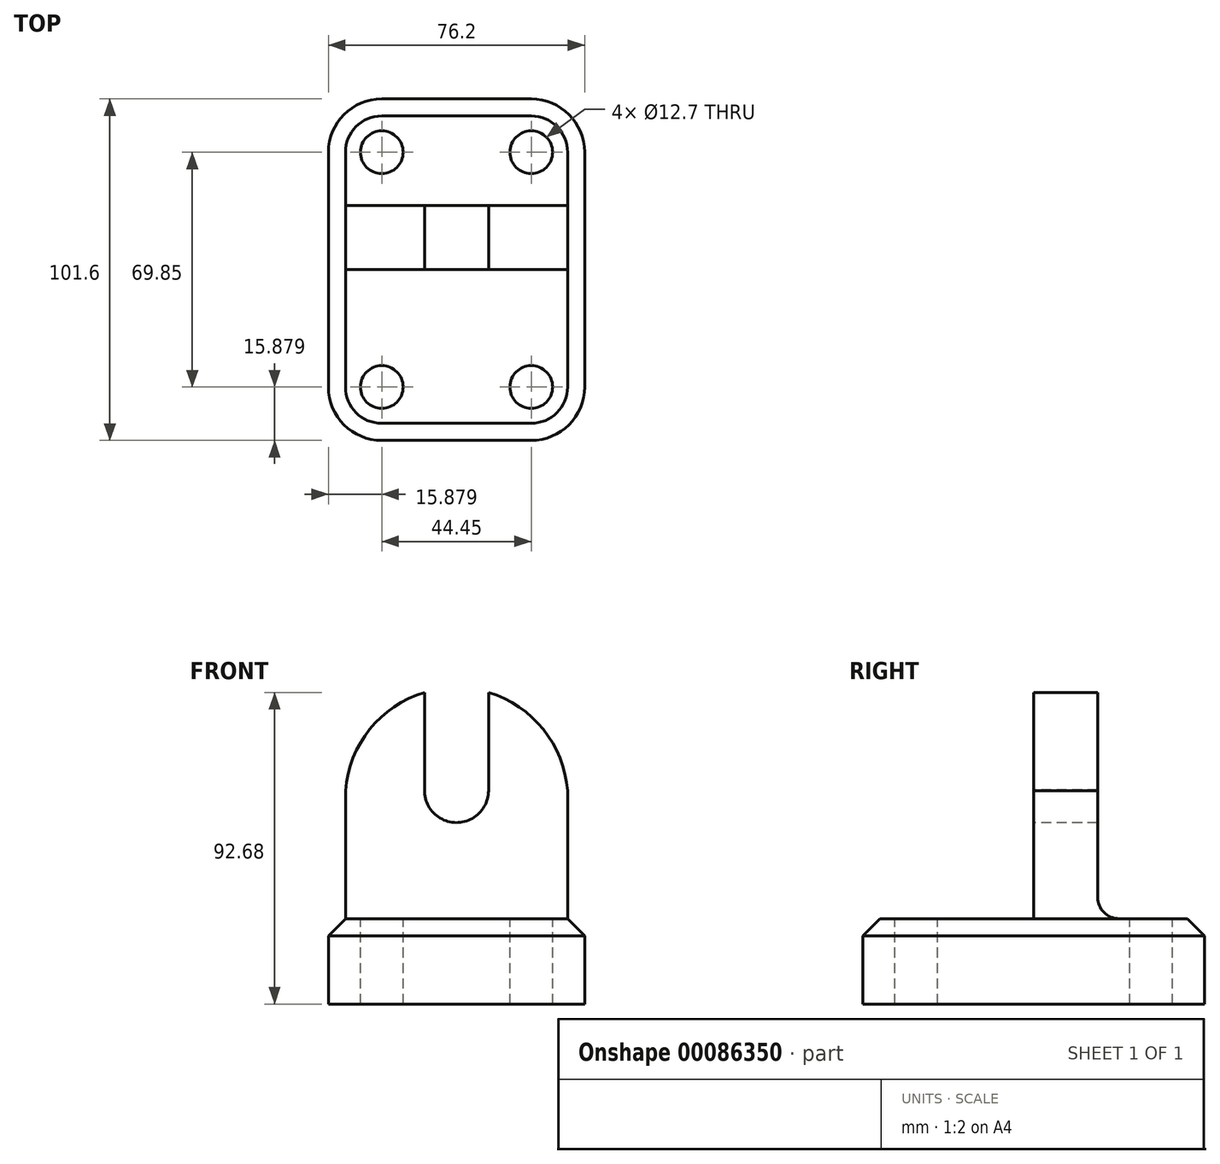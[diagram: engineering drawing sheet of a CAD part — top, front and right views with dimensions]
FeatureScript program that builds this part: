
annotation { "Feature Type Name" : "Feature", "Feature Type Description" : "" }
export const myFeature = defineFeature(function(context is Context, id is Id, definition is map)
    precondition{}
    {
        {
            var Q0;
            Q0=qCreatedBy(makeId("Top.planeOp"),FACE);
            var sketch = newSketch(context, id + "F0", { "sketchPlane" : qUnion([Q0])});
            skLineSegment(sketch, "E0.bottom", {"start": v(-19.44, 54.83) * mm, "end": v(56.76, 54.83) * mm});
            skLineSegment(sketch, "E0.top", {"start": v(-19.44, -46.77) * mm, "end": v(56.76, -46.77) * mm});
            skLineSegment(sketch, "E0.left", {"start": v(-19.44, 54.83) * mm, "end": v(-19.44, -46.77) * mm});
            skLineSegment(sketch, "E0.right", {"start": v(56.76, 54.83) * mm, "end": v(56.76, -46.77) * mm});
            skSolve(sketch);
        }
        {
            var Q0;
            Q0 = qSketchRegion(id + "F0", true);
            extrude(context, id + "F1", {"entities" : qUnion([Q0]), "depth" : 25.4 * mm});
        }
        {
            var Q0;
            Q0=makeQuery(id+"F1.opExtrude","SWEPT_EDGE",EDGE,{"disambiguationData":[OSD([sQuery(id+"F0.wireOp",EDGE,"E0.top"),sQuery(id+"F0.wireOp",EDGE,"E0.left")])]});
            var Q1;
            Q1=makeQuery(id+"F1.opExtrude","SWEPT_EDGE",EDGE,{"disambiguationData":[OSD([sQuery(id+"F0.wireOp",EDGE,"E0.top"),sQuery(id+"F0.wireOp",EDGE,"E0.right")])]});
            var Q2;
            Q2=makeQuery(id+"F1.opExtrude","SWEPT_EDGE",EDGE,{"disambiguationData":[OSD([sQuery(id+"F0.wireOp",EDGE,"E0.bottom"),sQuery(id+"F0.wireOp",EDGE,"E0.right")])]});
            var Q3;
            Q3=makeQuery(id+"F1.opExtrude","SWEPT_EDGE",EDGE,{"disambiguationData":[OSD([sQuery(id+"F0.wireOp",EDGE,"E0.bottom"),sQuery(id+"F0.wireOp",EDGE,"E0.left")])]});
            fillet(context, id + "F2", {"entities" : qUnion([Q0, Q1, Q2, Q3]), "radius" : 15.88 * mm, "tangentPropagation" : true, "allowEdgeOverflow" : false});
        }
        {
            var Q0;
            Q0=makeQuery(id+"F1.opExtrude","CAP_EDGE",EDGE,{"disambiguationData":[OSD([sQuery(id+"F0.wireOp",EDGE,"E0.bottom")])],"isStart":false});
            var Q1;
            {var subQ0=sQuery(id+"F0.wireOp",EDGE,"E0.left");var subQ1=sQuery(id+"F0.wireOp",EDGE,"E0.bottom");Q1=makeQuery(id+"F2.opFillet","BLEND_EDGE",EDGE,{"blendedFrom":[makeQuery(id+"F1.opExtrude","SWEPT_EDGE",EDGE,{"disambiguationData":[OSD([subQ1,subQ0])]}),makeQuery(id+"F1.opExtrude","CAP_FACE",FACE,{"disambiguationData":[OSD([subQ1,sQuery(id+"F0.wireOp",EDGE,"E0.top"),subQ0,sQuery(id+"F0.wireOp",EDGE,"E0.right")])],"isStart":false})],"blendedInto":[makeQuery(id+"F1.opExtrude","CAP_FACE",FACE,{"disambiguationData":[OSD([subQ1,sQuery(id+"F0.wireOp",EDGE,"E0.top"),subQ0,sQuery(id+"F0.wireOp",EDGE,"E0.right")])],"isStart":false})]});}
            var Q2;
            Q2=makeQuery(id+"F1.opExtrude","CAP_EDGE",EDGE,{"disambiguationData":[OSD([sQuery(id+"F0.wireOp",EDGE,"E0.left")])],"isStart":false});
            var Q3;
            {var subQ0=sQuery(id+"F0.wireOp",EDGE,"E0.left");var subQ1=sQuery(id+"F0.wireOp",EDGE,"E0.top");Q3=makeQuery(id+"F2.opFillet","BLEND_EDGE",EDGE,{"blendedFrom":[makeQuery(id+"F1.opExtrude","SWEPT_EDGE",EDGE,{"disambiguationData":[OSD([subQ1,subQ0])]}),makeQuery(id+"F1.opExtrude","CAP_FACE",FACE,{"disambiguationData":[OSD([sQuery(id+"F0.wireOp",EDGE,"E0.bottom"),subQ1,subQ0,sQuery(id+"F0.wireOp",EDGE,"E0.right")])],"isStart":false})],"blendedInto":[makeQuery(id+"F1.opExtrude","CAP_FACE",FACE,{"disambiguationData":[OSD([sQuery(id+"F0.wireOp",EDGE,"E0.bottom"),subQ1,subQ0,sQuery(id+"F0.wireOp",EDGE,"E0.right")])],"isStart":false})]});}
            var Q4;
            Q4=makeQuery(id+"F1.opExtrude","CAP_EDGE",EDGE,{"disambiguationData":[OSD([sQuery(id+"F0.wireOp",EDGE,"E0.top")])],"isStart":false});
            var Q5;
            {var subQ0=sQuery(id+"F0.wireOp",EDGE,"E0.right");var subQ1=sQuery(id+"F0.wireOp",EDGE,"E0.top");Q5=makeQuery(id+"F2.opFillet","BLEND_EDGE",EDGE,{"blendedFrom":[makeQuery(id+"F1.opExtrude","SWEPT_EDGE",EDGE,{"disambiguationData":[OSD([subQ1,subQ0])]}),makeQuery(id+"F1.opExtrude","CAP_FACE",FACE,{"disambiguationData":[OSD([sQuery(id+"F0.wireOp",EDGE,"E0.bottom"),subQ1,sQuery(id+"F0.wireOp",EDGE,"E0.left"),subQ0])],"isStart":false})],"blendedInto":[makeQuery(id+"F1.opExtrude","CAP_FACE",FACE,{"disambiguationData":[OSD([sQuery(id+"F0.wireOp",EDGE,"E0.bottom"),subQ1,sQuery(id+"F0.wireOp",EDGE,"E0.left"),subQ0])],"isStart":false})]});}
            var Q6;
            Q6=makeQuery(id+"F1.opExtrude","CAP_EDGE",EDGE,{"disambiguationData":[OSD([sQuery(id+"F0.wireOp",EDGE,"E0.right")])],"isStart":false});
            var Q7;
            {var subQ0=sQuery(id+"F0.wireOp",EDGE,"E0.right");var subQ1=sQuery(id+"F0.wireOp",EDGE,"E0.bottom");Q7=makeQuery(id+"F2.opFillet","BLEND_EDGE",EDGE,{"blendedFrom":[makeQuery(id+"F1.opExtrude","SWEPT_EDGE",EDGE,{"disambiguationData":[OSD([subQ1,subQ0])]}),makeQuery(id+"F1.opExtrude","CAP_FACE",FACE,{"disambiguationData":[OSD([subQ1,sQuery(id+"F0.wireOp",EDGE,"E0.top"),sQuery(id+"F0.wireOp",EDGE,"E0.left"),subQ0])],"isStart":false})],"blendedInto":[makeQuery(id+"F1.opExtrude","CAP_FACE",FACE,{"disambiguationData":[OSD([subQ1,sQuery(id+"F0.wireOp",EDGE,"E0.top"),sQuery(id+"F0.wireOp",EDGE,"E0.left"),subQ0])],"isStart":false})]});}
            chamfer(context, id + "F3", {"entities" : qUnion([Q0, Q1, Q2, Q3, Q4, Q5, Q6, Q7]), "width" : 5.08 * mm, "tangentPropagation" : true});
        }
        {
            var Q0;
            Q0=makeQuery(id+"F1.opExtrude","CAP_FACE",FACE,{"disambiguationData":[OSD([sQuery(id+"F0.wireOp",EDGE,"E0.bottom"),sQuery(id+"F0.wireOp",EDGE,"E0.top"),sQuery(id+"F0.wireOp",EDGE,"E0.left"),sQuery(id+"F0.wireOp",EDGE,"E0.right")])],"isStart":false});
            var sketch = newSketch(context, id + "F4", { "sketchPlane" : qUnion([Q0])});
            skCircle(sketch, "E1", {"center": v(-3.56, -30.9) * mm, "radius": 6.35 * mm});
            skCircle(sketch, "E2", {"center": v(-3.56, 38.96) * mm, "radius": 6.35 * mm});
            skCircle(sketch, "E3", {"center": v(40.89, 38.96) * mm, "radius": 6.35 * mm});
            skCircle(sketch, "E4", {"center": v(40.89, -30.9) * mm, "radius": 6.35 * mm});
            skSolve(sketch);
        }
        {
            var Q0;
            Q0 = qSketchRegion(id + "F4", true);
            extrude(context, id + "F5", {"entities" : qUnion([Q0]), "operationType" : NewBodyOperationType.REMOVE, "oppositeDirection" : true, "depth" : 25.4 * mm});
        }
        {
            var Q0;
            Q0=makeQuery(id+"F1.opExtrude","CAP_FACE",FACE,{"disambiguationData":[OSD([sQuery(id+"F0.wireOp",EDGE,"E0.bottom"),sQuery(id+"F0.wireOp",EDGE,"E0.top"),sQuery(id+"F0.wireOp",EDGE,"E0.left"),sQuery(id+"F0.wireOp",EDGE,"E0.right")])],"isStart":false});
            var sketch = newSketch(context, id + "F6", { "sketchPlane" : qUnion([Q0])});
            skLineSegment(sketch, "E5.bottom", {"start": v(-14.36, 23.08) * mm, "end": v(51.68, 23.08) * mm});
            skLineSegment(sketch, "E5.top", {"start": v(-14.36, 4.03) * mm, "end": v(51.68, 4.03) * mm});
            skLineSegment(sketch, "E5.left", {"start": v(-14.36, 23.08) * mm, "end": v(-14.36, 4.03) * mm});
            skLineSegment(sketch, "E5.right", {"start": v(51.68, 23.08) * mm, "end": v(51.68, 4.03) * mm});
            skSolve(sketch);
        }
        {
            var Q0;
            Q0 = qSketchRegion(id + "F6", true);
            extrude(context, id + "F7", {"entities" : qUnion([Q0]), "operationType" : NewBodyOperationType.ADD, "depth" : 38.1 * mm});
        }
        {
            var Q0;
            Q0=makeQuery(id+"F7.opExtrude","SWEPT_FACE",FACE,{"disambiguationData":[OSD([sQuery(id+"F6.wireOp",EDGE,"E5.top")])]});
            var sketch = newSketch(context, id + "F8", { "sketchPlane" : qUnion([Q0])});
            skArc(sketch, "E6", {"start": v(51.68, 63.5) * mm, "mid": v(18.66, 94.08) * mm, "end": v(-14.36, 63.5) * mm});
            skSolve(sketch);
        }
        {
            var Q0;
            Q0=makeQuery(id+"F8.imprint","IMPRINT",FACE,{"disambiguationData":[TD([[makeQuery(id+"F8.imprint","IMPRINT",EDGE,{"derivedFrom":sQuery(id+"F8.wireOp",EDGE,"E6")}),1.0]])]});
            extrude(context, id + "F9", {"entities" : qUnion([Q0]), "operationType" : NewBodyOperationType.ADD, "oppositeDirection" : true, "depth" : 19.05 * mm});
        }
        {
            var Q0;
            {var subQ0=sQuery(id+"F6.wireOp",EDGE,"E5.top");Q0=makeQuery(id+"F9.boolean.opBoolean","MERGE",FACE,{"derivedFrom":[makeQuery(id+"F7.opExtrude","SWEPT_FACE",FACE,{"disambiguationData":[OSD([subQ0])]}),makeQuery(id+"F9.opExtrude","CAP_FACE",FACE,{"disambiguationData":[OSD([subQ0,sQuery(id+"F8.wireOp",EDGE,"E6")])],"isStart":true})]});}
            var sketch = newSketch(context, id + "F10", { "sketchPlane" : qUnion([Q0])});
            skCircle(sketch, "E7", {"center": v(18.66, 63.5) * mm, "radius": 9.53 * mm});
            skSolve(sketch);
        }
        {
            var Q0;
            Q0 = qSketchRegion(id + "F10", true);
            extrude(context, id + "F11", {"entities" : qUnion([Q0]), "operationType" : NewBodyOperationType.REMOVE, "oppositeDirection" : true, "depth" : 25.4 * mm});
        }
        {
            var Q0;
            {var subQ0=sQuery(id+"F6.wireOp",EDGE,"E5.top");Q0=makeQuery(id+"F9.boolean.opBoolean","MERGE",FACE,{"derivedFrom":[makeQuery(id+"F7.opExtrude","SWEPT_FACE",FACE,{"disambiguationData":[OSD([subQ0])]}),makeQuery(id+"F9.opExtrude","CAP_FACE",FACE,{"disambiguationData":[OSD([subQ0,sQuery(id+"F8.wireOp",EDGE,"E6")])],"isStart":true})]});}
            var sketch = newSketch(context, id + "F12", { "sketchPlane" : qUnion([Q0])});
            skLineSegment(sketch, "E8.left", {"start": v(9.14, 63.3) * mm, "end": v(9.14, 63.5) * mm});
            skLineSegment(sketch, "E8.right", {"start": v(28.19, 63.3) * mm, "end": v(28.19, 63.5) * mm});
            skLineSegment(sketch, "E9.bottom", {"start": v(9.14, 63.5) * mm, "end": v(28.23, 63.5) * mm});
            skLineSegment(sketch, "E9.top", {"start": v(9.14, 94.58) * mm, "end": v(28.23, 94.58) * mm});
            skLineSegment(sketch, "E9.left", {"start": v(9.14, 63.5) * mm, "end": v(9.14, 94.58) * mm});
            skLineSegment(sketch, "E9.right", {"start": v(28.23, 63.5) * mm, "end": v(28.23, 94.58) * mm});
            skSolve(sketch);
        }
        {
            var Q0;
            Q0 = qSketchRegion(id + "F12", true);
            extrude(context, id + "F13", {"entities" : qUnion([Q0]), "operationType" : NewBodyOperationType.REMOVE, "oppositeDirection" : true, "depth" : 25.4 * mm});
        }
        {
            var Q0;
            Q0=makeQuery(id+"F7.opExtrude","CAP_EDGE",EDGE,{"disambiguationData":[OSD([sQuery(id+"F6.wireOp",EDGE,"E5.top")])],"isStart":true});
            var Q1;
            Q1=makeQuery(id+"F7.opExtrude","CAP_EDGE",EDGE,{"disambiguationData":[OSD([sQuery(id+"F6.wireOp",EDGE,"E5.bottom")])],"isStart":true});
            fillet(context, id + "F14", {"entities" : qUnion([Q0, Q1]), "radius" : 6.35 * mm, "tangentPropagation" : true, "allowEdgeOverflow" : false});
        }
    });
